# Revit family: Plumbing_Drainage_AXOR_42520CHN-AXOR-Drain-Finish-set-shower-dr_NEW
name_source: partatom
category: Plumbing Fixtures
revit_build: Autodesk Revit 2018 (Build: 20170223_1515(x64)
units: mm (PartAtom-declared; Revit-internal decimal feet)

## family parameters
Cut with Voids When Loaded = Yes
Host = Face
OmniClass Number = 23.31.17.29
OmniClass Title = Shower Drains
Part Type = Normal
Room Calculation Point = No
Round Connector Dimension = Use Diameter
Shared = No

## types (5) — shared parameters
BIMobject category = Drainage
Default Elevation = 1219 mm
Description = AXOR Drain Finish set shower drain 700
Design country = Germany
Edition number = 1
IFC Classification = Sanitary Terminal
Manufacturer = AXOR
Manufacturer country = Germany
Manufacturer name = AXOR
Material 1 = AXOR - Plastic - Dark Grey
Material 2 = AXOR - Plastic - Grey
Model = 42520CHN
OmniClass Code = 23-31 17 29
OmniClass Description = Shower Drains
Product Guid = aa2fd6e2-e0f2-44c7-8dcd-3a79b8a877ad
Product SKU = 42520CHN
Product data url = https://bimobject.com
Product name = 42520CHN AXOR Drain Finish set shower drain 700
Product url = https://www.axor-design.com
QR code = https://bimobject.com
URL = https://www.axor-design.com

## per-type parameters (varying)
| type | Material 3 |
| 007 Chrome | AXOR - Metal - 007 Chrome |
| 347 Brushed Black Chrome | AXOR - Metal - 347 Brushed Black Chrome |
| 677 Matte Black | AXOR - Metal - 677 Matte Black |
| 707 Matte White | AXOR - Metal - 707 Matte White |
| 997 Polished Gold Optic | AXOR - Metal - 997 Polished Gold Optic |

## geometry (parser evidence)
native form markers: Sweep x6
no freeform markers — native parametric forms only
